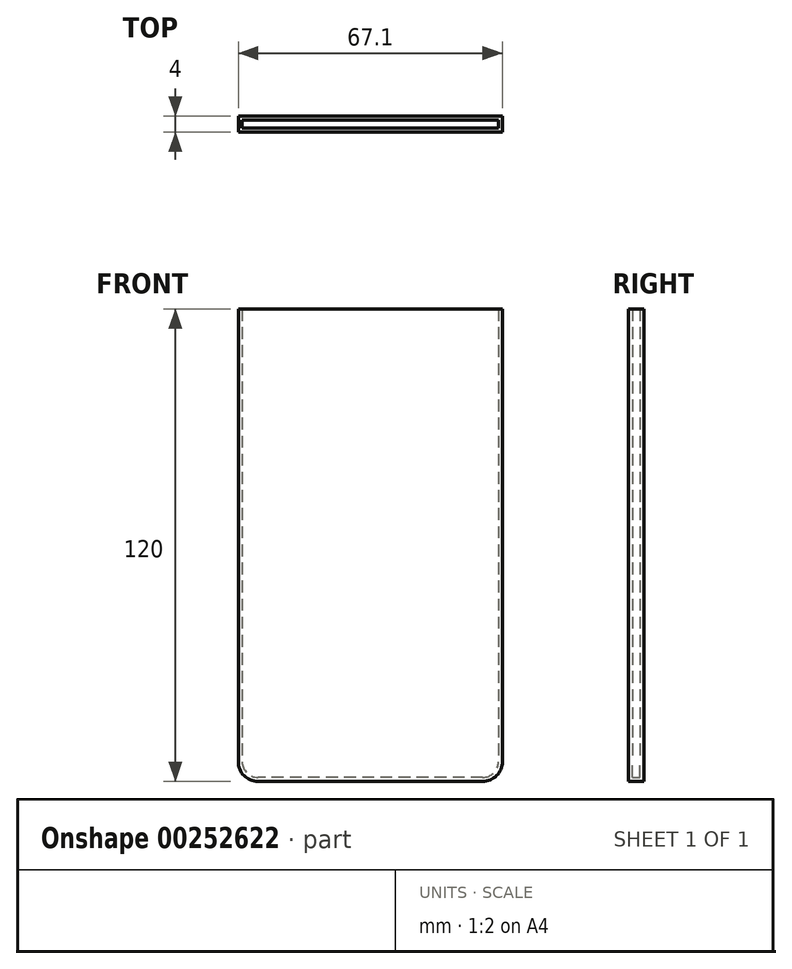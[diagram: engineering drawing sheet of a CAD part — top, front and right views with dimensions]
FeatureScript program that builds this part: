
annotation { "Feature Type Name" : "Feature", "Feature Type Description" : "" }
export const myFeature = defineFeature(function(context is Context, id is Id, definition is map)
    precondition{}
    {
        {
            var Q0;
            Q0=qCreatedBy(makeId("Front.planeOp"),FACE);
            var sketch = newSketch(context, id + "F0", { "sketchPlane" : qUnion([Q0])});
            skLineSegment(sketch, "E0.bottom", {"start": v(33.55, 60) * mm, "end": v(-33.55, 60) * mm});
            skLineSegment(sketch, "E0.top", {"start": v(33.55, -60) * mm, "end": v(-33.55, -60) * mm});
            skLineSegment(sketch, "E0.left", {"start": v(33.55, 60) * mm, "end": v(33.55, -60) * mm});
            skLineSegment(sketch, "E0.right", {"start": v(-33.55, 60) * mm, "end": v(-33.55, -60) * mm});
            skPoint(sketch, "E0.middle", {"position": v(0, 0) * mm});
            skSolve(sketch);
        }
        {
            var Q0;
            Q0 = qSketchRegion(id + "F0", true);
            extrude(context, id + "F1", {"entities" : qUnion([Q0]), "depth" : 4 * mm});
        }
        {
            var Q0;
            Q0=makeQuery(id+"F1.opExtrude","SWEPT_EDGE",EDGE,{"disambiguationData":[OSD([sQuery(id+"F0.wireOp",EDGE,"E0.top"),sQuery(id+"F0.wireOp",EDGE,"E0.left")])]});
            var Q1;
            Q1=makeQuery(id+"F1.opExtrude","SWEPT_EDGE",EDGE,{"disambiguationData":[OSD([sQuery(id+"F0.wireOp",EDGE,"E0.top"),sQuery(id+"F0.wireOp",EDGE,"E0.right")])]});
            fillet(context, id + "F2", {"entities" : qUnion([Q0, Q1]), "radius" : 5 * mm, "tangentPropagation" : true, "allowEdgeOverflow" : false});
        }
        {
            var Q0;
            Q0=makeQuery(id+"F1.opExtrude","SWEPT_FACE",FACE,{"disambiguationData":[OSD([sQuery(id+"F0.wireOp",EDGE,"E0.bottom")])]});
            shell(context, id + "F3", {"entities" : qUnion([Q0]), "thickness" : 1 * mm});
        }
    });
